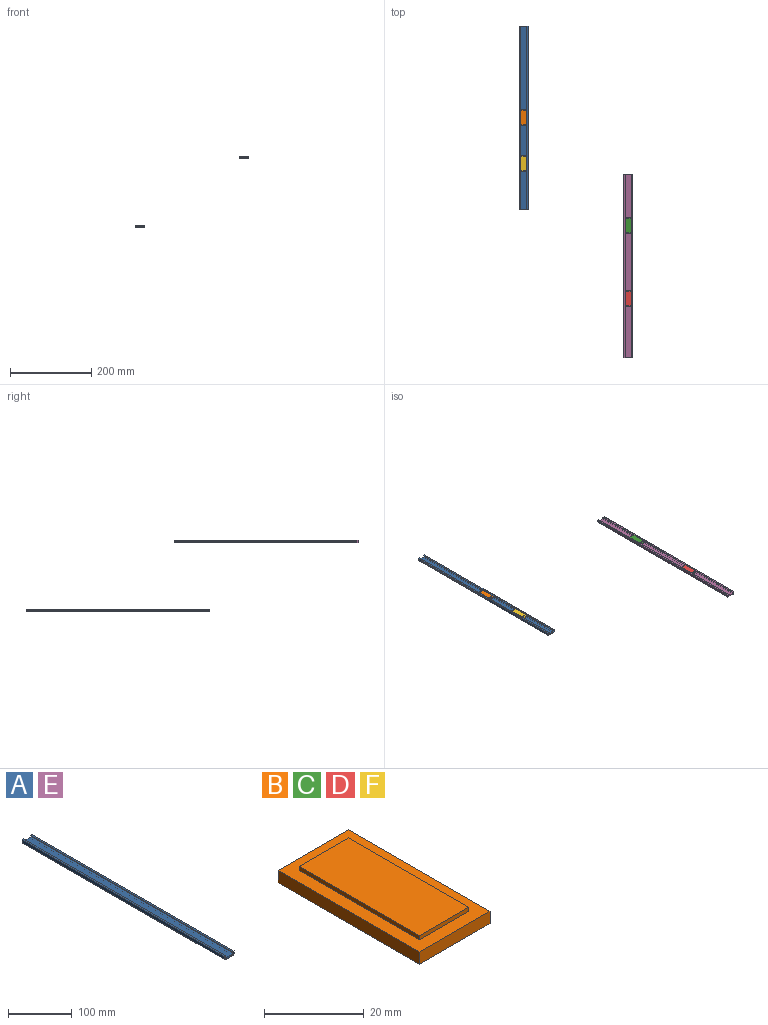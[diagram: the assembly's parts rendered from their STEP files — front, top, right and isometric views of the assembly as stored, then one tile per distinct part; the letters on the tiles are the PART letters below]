
ASSEMBLY  parts=6 mates=5
PART A: 22 faces, bbox 22x450x7 mm
  f0: plane 450x5mm, normal (0,0,-1), area 2250mm2, adj f1,f19,f20,f21
  f1: plane 450x1mm, normal (-1,0,0), area 450mm2, adj f0,f2,f20,f21
  f2: plane 450x3mm, normal (0,0,1), area 1350mm2, adj f1,f3,f20,f21
  f3: plane 450x1mm, normal (-1,0,0), area 450mm2, adj f2,f4,f20,f21
  f4: plane 450x18mm, normal (0,0,-1), area 8100mm2, adj f3,f5,f20,f21
  f5: plane 450x1mm, normal (1,0,0), area 450mm2, adj f4,f6,f20,f21
  f6: plane 450x3mm, normal (0,0,1), area 1350mm2, adj f5,f7,f20,f21
  f7: plane 450x1mm, normal (1,0,0), area 450mm2, adj f6,f8,f20,f21
  f8: plane 450x5mm, normal (0,0,-1), area 2250mm2, adj f7,f9,f20,f21
  f9: plane 450x5mm, normal (1,0,0), area 2250mm2, adj f8,f10,f20,f21
  f10: plane 450x4mm, normal (0,0,1), area 1800mm2, adj f9,f11,f20,f21
  f11: plane 450x1mm, normal (-1,0,0), area 450mm2, adj f10,f12,f20,f21
  f12: plane 450x3mm, normal (0,0,-1), area 1350mm2, adj f11,f13,f20,f21
  f13: plane 450x3mm, normal (-1,0,0), area 1350mm2, adj f12,f14,f20,f21
  f14: plane 450x20mm, normal (0,0,1), area 9000mm2, adj f13,f15,f20,f21
  f15: plane 450x3mm, normal (1,0,0), area 1350mm2, adj f14,f16,f20,f21
  f16: plane 450x3mm, normal (0,0,-1), area 1350mm2, adj f15,f17,f20,f21
  f17: plane 450x1mm, normal (1,0,0), area 450mm2, adj f16,f18,f20,f21
  f18: plane 450x4mm, normal (0,0,1), area 1800mm2, adj f17,f19,f20,f21
  f19: plane 450x5mm, normal (-1,0,0), area 2250mm2, adj f0,f18,f20,f21
  f20: plane 22x7mm, normal (0,-1,0), area 66mm2, adj f0,f1,f2,f3,f4,f5,f6,f7
  f21: plane 22x7mm, normal (0,1,0), area 66mm2, adj f0,f1,f2,f3,f4,f5,f6,f7
PART B: 11 faces, bbox 20x40x4 mm
  f0: plane 40x20mm, normal (0,0,1), area 324mm2, adj f1,f2,f3,f4,f6,f7,f8,f9
  f1: plane 20x3mm, normal (0,1,0), area 60mm2, adj f0,f2,f4,f5
  f2: plane 40x3mm, normal (-1,0,0), area 120mm2, adj f0,f1,f3,f5
  f3: plane 20x3mm, normal (0,-1,0), area 60mm2, adj f0,f2,f4,f5
  f4: plane 40x3mm, normal (1,0,0), area 120mm2, adj f0,f1,f3,f5
  f5: plane 40x20mm, normal (0,0,-1), area 800mm2, adj f1,f2,f3,f4
  f6: plane 14x1mm, normal (0,1,0), area 14mm2, adj f0,f7,f9,f10
  f7: plane 34x1mm, normal (-1,0,0), area 34mm2, adj f0,f6,f8,f10
  f8: plane 14x1mm, normal (0,-1,0), area 14mm2, adj f0,f7,f9,f10
  f9: plane 34x1mm, normal (1,0,0), area 34mm2, adj f0,f6,f8,f10
  f10: plane 34x14mm, normal (0,0,1), area 476mm2, adj f6,f7,f8,f9
PART C: same geometry as B
PART D: same geometry as B
PART E: same geometry as A
PART F: same geometry as B
PLACE A t=(-131.93,555.78,-111.63)mm fixed
PLACE B t=(-131.93,332.06,-113.13)mm
PLACE C t=(125.37,65.6,56.38)mm
PLACE D t=(125.37,-113.77,56.38)mm
PLACE E t=(125.37,190.55,57.88)mm fixed
PLACE F t=(-131.93,218.32,-113.13)mm
MATE planar E.f14 <-> C.f5  axis (0,0,1) through (125.37,190.55,56.38)mm
MATE slider A.f21 <-> F.f1  axis (0,1,0) through (-131.93,555.78,-113.13)mm
MATE planar F.f4 <-> A.f13  axis (1,0,0) through (-121.93,198.32,-111.63)mm
MATE planar A.f14 <-> F.f5  axis (0,0,1) through (-131.93,330.78,-113.13)mm
MATE planar E.f14 <-> D.f5  axis (0,0,1) through (125.37,-34.45,56.38)mm
